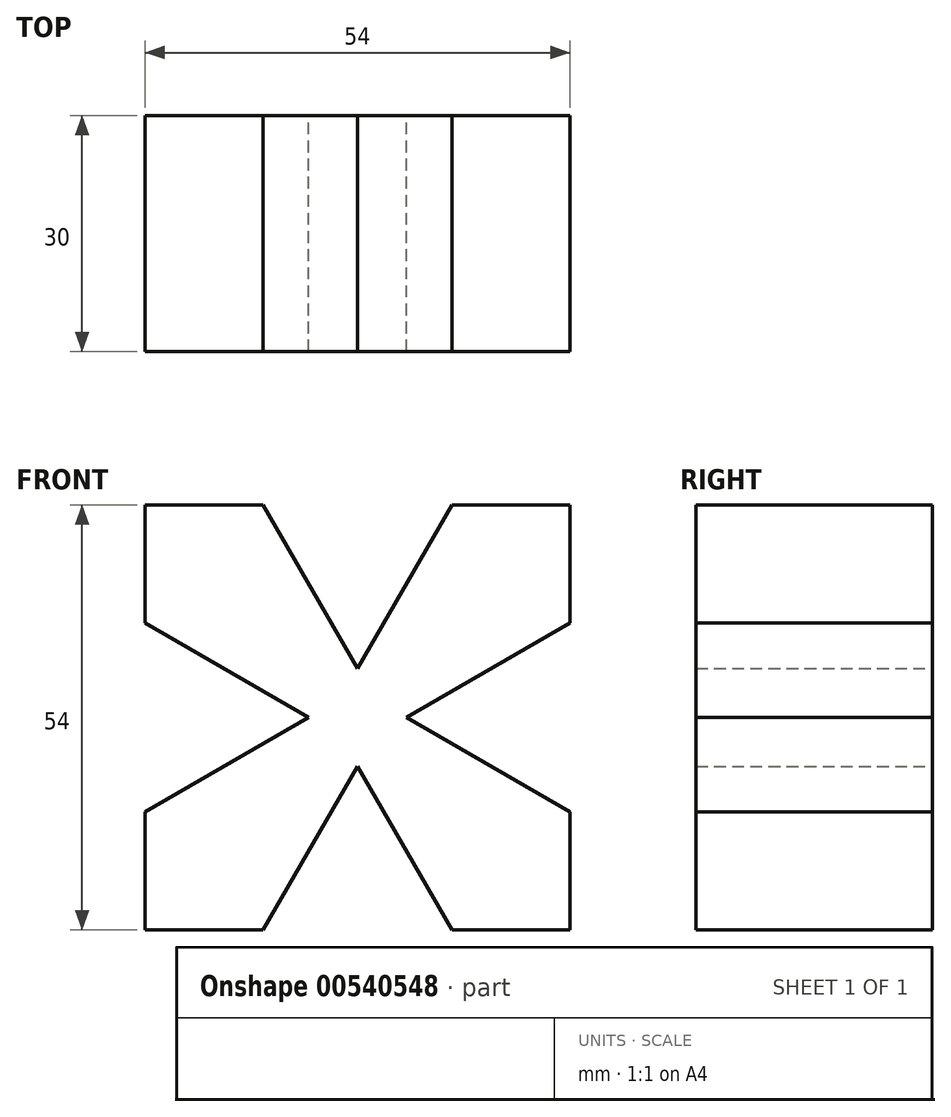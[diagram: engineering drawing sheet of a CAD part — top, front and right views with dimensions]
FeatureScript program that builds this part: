
annotation { "Feature Type Name" : "Feature", "Feature Type Description" : "" }
export const myFeature = defineFeature(function(context is Context, id is Id, definition is map)
    precondition{}
    {
        {
            var Q0;
            Q0=qCreatedBy(makeId("Front.planeOp"),FACE);
            var sketch = newSketch(context, id + "F0", { "sketchPlane" : qUnion([Q0])});
            skLineSegment(sketch, "E0.bottom", {"start": v(-27, 26.11) * mm, "end": v(-12, 26.11) * mm});
            skLineSegment(sketch, "E0.top", {"start": v(-27, -27.89) * mm, "end": v(-12, -27.89) * mm});
            skLineSegment(sketch, "E0.right", {"start": v(27, 26.11) * mm, "end": v(27, 11.11) * mm});
            skLineSegment(sketch, "E1", {"start": v(-27, -27.89) * mm, "end": v(-27, -12.89) * mm});
            skLineSegment(sketch, "E2", {"start": v(27, -27.89) * mm, "end": v(12, -27.89) * mm});
            skLineSegment(sketch, "E3", {"start": v(27, -27.89) * mm, "end": v(27, -12.89) * mm});
            skLineSegment(sketch, "E4", {"start": v(27, 26.11) * mm, "end": v(12, 26.11) * mm});
            skLineSegment(sketch, "E5", {"start": v(-27, 26.11) * mm, "end": v(-27, 11.11) * mm});
            skLineSegment(sketch, "E6", {"start": v(-12, -27.89) * mm, "end": v(0, -7.1) * mm});
            skLineSegment(sketch, "E7", {"start": v(12, -27.89) * mm, "end": v(0, -7.1) * mm});
            skLineSegment(sketch, "E8", {"start": v(-27, -12.89) * mm, "end": v(-6.22, -0.89) * mm});
            skLineSegment(sketch, "E9", {"start": v(27, -12.89) * mm, "end": v(6.22, -0.89) * mm});
            skLineSegment(sketch, "E10", {"start": v(-6.22, -0.89) * mm, "end": v(-27, 11.11) * mm});
            skLineSegment(sketch, "E11", {"start": v(6.22, -0.89) * mm, "end": v(27, 11.11) * mm});
            skLineSegment(sketch, "E12", {"start": v(-12, 26.11) * mm, "end": v(0, 5.33) * mm});
            skLineSegment(sketch, "E13", {"start": v(12, 26.11) * mm, "end": v(0, 5.33) * mm});
            skLineSegment(sketch, "E14.trimOffspring", {"start": v(-27, -12.89) * mm, "end": v(-27, -27.89) * mm});
            skLineSegment(sketch, "E15.trimOffspring", {"start": v(27, -12.89) * mm, "end": v(27, -27.89) * mm});
            skLineSegment(sketch, "E16.trimOffspring", {"start": v(12, 26.11) * mm, "end": v(27, 26.11) * mm});
            skLineSegment(sketch, "E17.trimOffspring", {"start": v(12, -27.89) * mm, "end": v(27, -27.89) * mm});
            skSolve(sketch);
        }
        {
            var Q0;
            Q0 = qSketchRegion(id + "F0", true);
            extrude(context, id + "F1", {"entities" : qUnion([Q0]), "depth" : 30 * mm, "offsetDistance" : 25 * mm});
        }
    });
